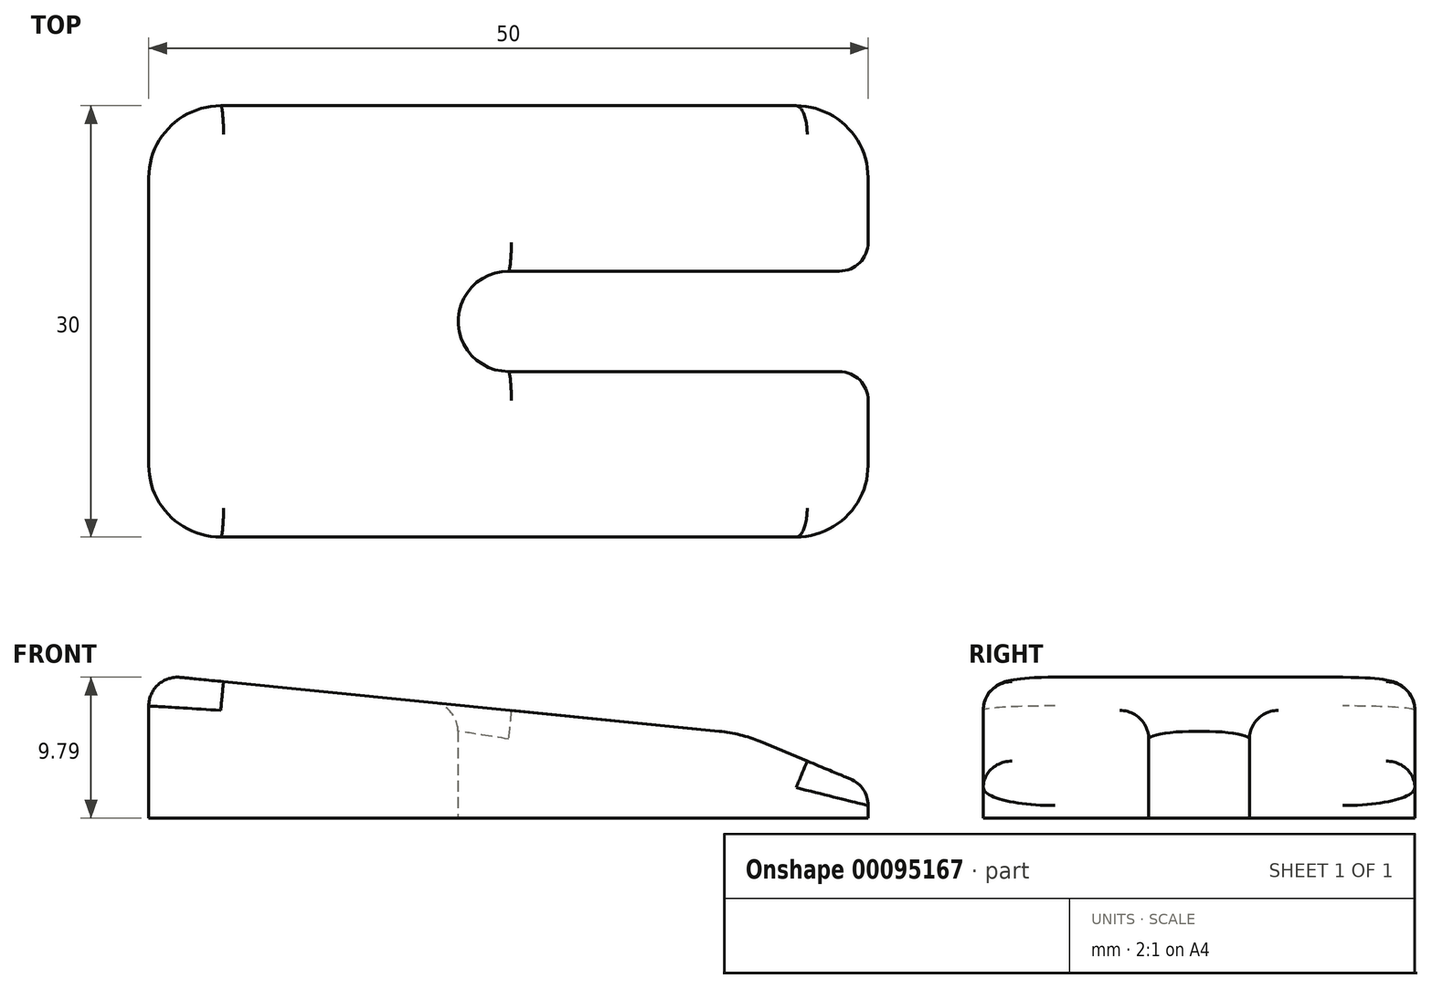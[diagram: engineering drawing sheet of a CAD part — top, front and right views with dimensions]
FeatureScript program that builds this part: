
annotation { "Feature Type Name" : "Feature", "Feature Type Description" : "" }
export const myFeature = defineFeature(function(context is Context, id is Id, definition is map)
    precondition{}
    {
        {
            var Q0;
            Q0=qCreatedBy(makeId("Top.planeOp"),FACE);
            var sketch = newSketch(context, id + "F0", { "sketchPlane" : qUnion([Q0])});
            skLineSegment(sketch, "E0.bottom", {"start": v(0, 0) * mm, "end": v(50, 0) * mm});
            skLineSegment(sketch, "E0.top", {"start": v(0, 30) * mm, "end": v(50, 30) * mm});
            skLineSegment(sketch, "E0.left", {"start": v(0, 0) * mm, "end": v(0, 30) * mm});
            skLineSegment(sketch, "E0.right", {"start": v(50, 0) * mm, "end": v(50, 30) * mm});
            skArc(sketch, "E1", {"start": v(25, 18.5) * mm, "mid": v(21.5, 15) * mm, "end": v(25, 11.5) * mm});
            skLineSegment(sketch, "E2.bottom", {"start": v(25, 18.5) * mm, "end": v(50, 18.5) * mm});
            skLineSegment(sketch, "E2.top", {"start": v(25, 11.5) * mm, "end": v(50, 11.5) * mm});
            skSolve(sketch);
        }
        {
            var Q0;
            {var subQ1=sQuery(id+"F0.wireOp",EDGE,"E0.bottom");Q0=makeQuery(id+"F0.imprint","IMPRINT",FACE,{"disambiguationData":[TD([[makeQuery(id+"F0.imprint","IMPRINT",EDGE,{"derivedFrom":subQ1}),1.0]])]});}
            extrude(context, id + "F1", {"entities" : qUnion([Q0]), "depth" : 10 * mm});
        }
        {
            var Q0;
            Q0=makeQuery(id+"F1.opExtrude","SWEPT_FACE",FACE,{"disambiguationData":[OSD([sQuery(id+"F0.wireOp",EDGE,"E0.bottom")])]});
            var sketch = newSketch(context, id + "F2", { "sketchPlane" : qUnion([Q0])});
            skLineSegment(sketch, "E3", {"start": v(0, 10) * mm, "end": v(39.66, 6.03) * mm});
            skPoint(sketch, "E4.orphan", {"position": v(50, 5) * mm});
            skPoint(sketch, "E5.visualSharp", {"position": v(42.48, 5.75) * mm});
            skArc(sketch, "E5.filletArc", {"start": v(42.5, 5.32) * mm, "mid": v(41.1, 5.78) * mm, "end": v(39.66, 6.03) * mm});
            skLineSegment(sketch, "E6", {"start": v(42.5, 5.32) * mm, "end": v(50, 2.2) * mm});
            skSolve(sketch);
        }
        {
            var Q0;
            {var subQ0=sQuery(id+"F2.wireOp",EDGE,"E3");Q0=makeQuery(id+"F2.imprint","IMPRINT",FACE,{"disambiguationData":[TD([[makeQuery(id+"F2.imprint","IMPRINT",EDGE,{"derivedFrom":subQ0}),1.0]])]});}
            extrude(context, id + "F3", {"entities" : qUnion([Q0]), "operationType" : NewBodyOperationType.REMOVE, "oppositeDirection" : true, "depth" : 30 * mm});
        }
        {
            var Q0;
            Q0=makeQuery(id+"F1.opExtrude","SWEPT_EDGE",EDGE,{"disambiguationData":[OSD([sQuery(id+"F0.wireOp",EDGE,"E0.top"),sQuery(id+"F0.wireOp",EDGE,"E0.left")])]});
            var Q1;
            Q1=makeQuery(id+"F1.opExtrude","SWEPT_EDGE",EDGE,{"disambiguationData":[OSD([sQuery(id+"F0.wireOp",EDGE,"E0.bottom"),sQuery(id+"F0.wireOp",EDGE,"E0.left")])]});
            var Q2;
            Q2=makeQuery(id+"F1.opExtrude","SWEPT_EDGE",EDGE,{"disambiguationData":[OSD([sQuery(id+"F0.wireOp",EDGE,"E0.bottom"),sQuery(id+"F0.wireOp",EDGE,"E0.right")])]});
            var Q3;
            Q3=makeQuery(id+"F1.opExtrude","SWEPT_EDGE",EDGE,{"disambiguationData":[OSD([sQuery(id+"F0.wireOp",EDGE,"E0.top"),sQuery(id+"F0.wireOp",EDGE,"E0.right")])]});
            fillet(context, id + "F4", {"entities" : qUnion([Q0, Q1, Q2, Q3]), "radius" : 5 * mm, "tangentPropagation" : true, "allowEdgeOverflow" : false});
        }
        {
            var Q0;
            Q0=makeQuery(id+"F4.opFillet","BLEND_EDGE",EDGE,{"blendedFrom":[makeQuery(id+"F1.opExtrude","SWEPT_EDGE",EDGE,{"disambiguationData":[OSD([sQuery(id+"F0.wireOp",EDGE,"E0.top"),sQuery(id+"F0.wireOp",EDGE,"E0.left")])]}),makeQuery(id+"F3.boolean.opBoolean","COPY",FACE,{"derivedFrom":makeQuery(id+"F3.opExtrude","SWEPT_FACE",FACE,{"disambiguationData":[OSD([sQuery(id+"F2.wireOp",EDGE,"E3")])]})})],"blendedInto":[makeQuery(id+"F3.boolean.opBoolean","COPY",FACE,{"derivedFrom":makeQuery(id+"F3.opExtrude","SWEPT_FACE",FACE,{"disambiguationData":[OSD([sQuery(id+"F2.wireOp",EDGE,"E3")])]})})]});
            var Q1;
            Q1=makeQuery(id+"F3.boolean.opBoolean","INTERSECT",EDGE,{"derivedFrom":[makeQuery(id+"F1.opExtrude","SWEPT_FACE",FACE,{"disambiguationData":[OSD([sQuery(id+"F0.wireOp",EDGE,"E2.top")])]}),makeQuery(id+"F3.opExtrude","SWEPT_FACE",FACE,{"disambiguationData":[OSD([sQuery(id+"F2.wireOp",EDGE,"E3")])]})]});
            var Q2;
            Q2=makeQuery(id+"F1.opExtrude","SWEPT_EDGE",EDGE,{"disambiguationData":[OSD([sQuery(id+"F0.wireOp",EDGE,"E0.right"),sQuery(id+"F0.wireOp",EDGE,"E2.top")])]});
            var Q3;
            Q3=makeQuery(id+"F1.opExtrude","SWEPT_EDGE",EDGE,{"disambiguationData":[OSD([sQuery(id+"F0.wireOp",EDGE,"E0.right"),sQuery(id+"F0.wireOp",EDGE,"E2.bottom")])]});
            fillet(context, id + "F5", {"entities" : qUnion([Q0, Q1, Q2, Q3]), "radius" : 2 * mm, "tangentPropagation" : true, "allowEdgeOverflow" : false});
        }
    });
